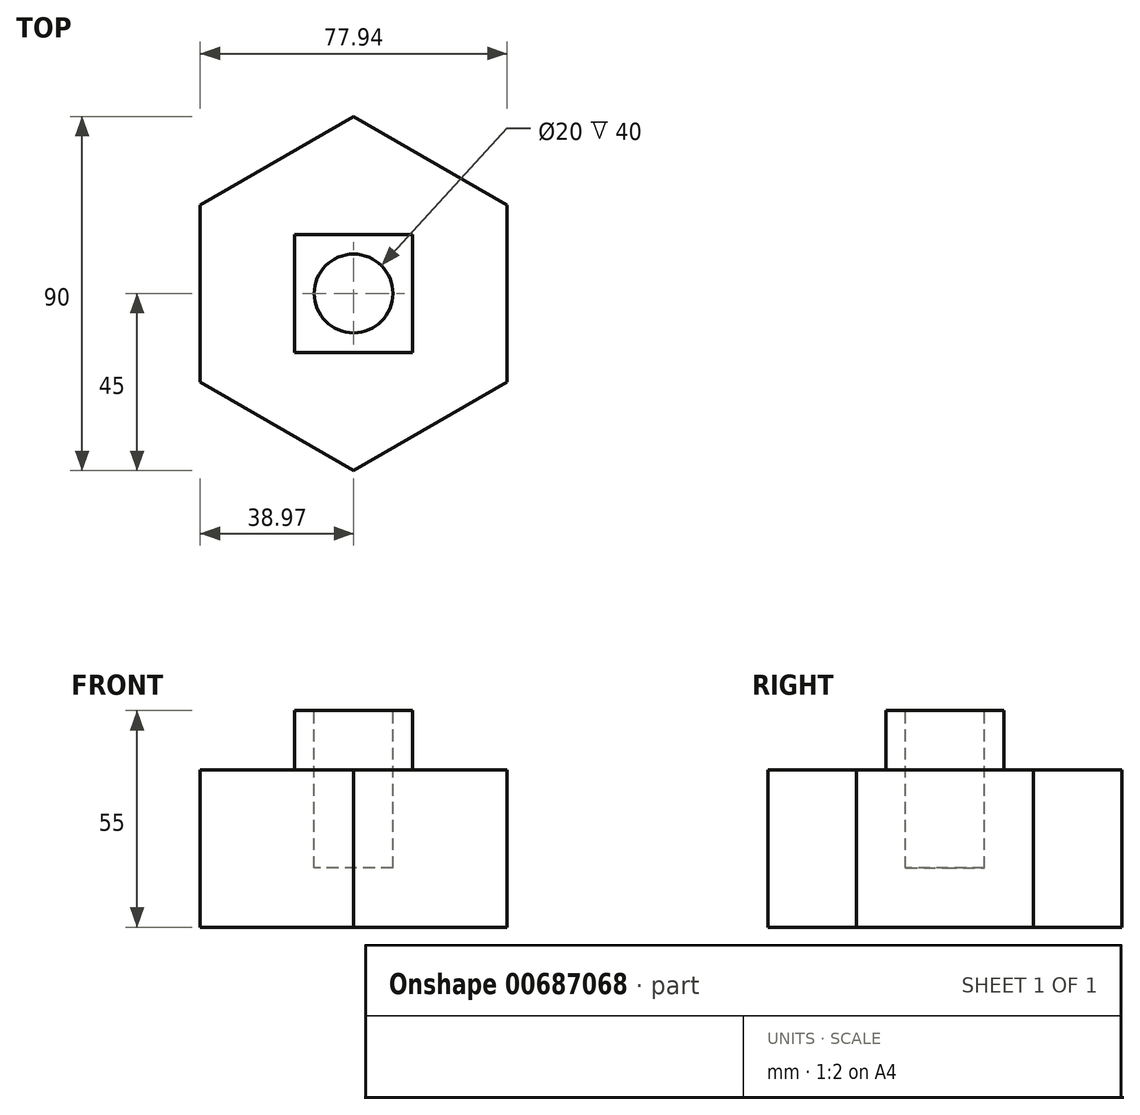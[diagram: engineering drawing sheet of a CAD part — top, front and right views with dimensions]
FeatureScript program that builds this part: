
annotation { "Feature Type Name" : "Feature", "Feature Type Description" : "" }
export const myFeature = defineFeature(function(context is Context, id is Id, definition is map)
    precondition{}
    {
        {
            var Q0;
            Q0=qCreatedBy(makeId("Top.planeOp"),FACE);
            var sketch = newSketch(context, id + "F0", { "sketchPlane" : qUnion([Q0])});
            skCircle(sketch, "E0.cCircle", {"center": v(0, 0) * mm, "radius": 38.97 * mm, "construction": true});
            skLineSegment(sketch, "E0.0", {"start": v(38.97, 22.5) * mm, "end": v(38.97, -22.5) * mm});
            skLineSegment(sketch, "E0.1", {"start": v(38.97, -22.5) * mm, "end": v(0, -45) * mm});
            skLineSegment(sketch, "E0.2", {"start": v(0, -45) * mm, "end": v(-38.97, -22.5) * mm});
            skLineSegment(sketch, "E0.3", {"start": v(-38.97, -22.5) * mm, "end": v(-38.97, 22.5) * mm});
            skLineSegment(sketch, "E0.4", {"start": v(-38.97, 22.5) * mm, "end": v(0, 45) * mm});
            skLineSegment(sketch, "E0.5", {"start": v(0, 45) * mm, "end": v(38.97, 22.5) * mm});
            skPoint(sketch, "E0.0.midPoint", {"position": v(38.97, 0) * mm});
            skSolve(sketch);
        }
        {
            var Q0;
            Q0 = qSketchRegion(id + "F0", true);
            extrude(context, id + "F1", {"entities" : qUnion([Q0]), "depth" : 40 * mm, "offsetDistance" : 25 * mm});
        }
        {
            var Q0;
            Q0=makeQuery(id+"F1.opExtrude","CAP_FACE",FACE,{"disambiguationData":[OSD([sQuery(id+"F0.wireOp",EDGE,"E0.0"),sQuery(id+"F0.wireOp",EDGE,"E0.1"),sQuery(id+"F0.wireOp",EDGE,"E0.2"),sQuery(id+"F0.wireOp",EDGE,"E0.3"),sQuery(id+"F0.wireOp",EDGE,"E0.4"),sQuery(id+"F0.wireOp",EDGE,"E0.5")])],"isStart":false});
            var sketch = newSketch(context, id + "F2", { "sketchPlane" : qUnion([Q0])});
            skLineSegment(sketch, "E1.bottom", {"start": v(15, 15) * mm, "end": v(-15, 15) * mm});
            skLineSegment(sketch, "E1.top", {"start": v(15, -15) * mm, "end": v(-15, -15) * mm});
            skLineSegment(sketch, "E1.left", {"start": v(15, 15) * mm, "end": v(15, -15) * mm});
            skLineSegment(sketch, "E1.right", {"start": v(-15, 15) * mm, "end": v(-15, -15) * mm});
            skPoint(sketch, "E1.middle", {"position": v(0, 0) * mm});
            skSolve(sketch);
        }
        {
            var Q0;
            Q0=makeQuery(id+"F2.imprint","IMPRINT",FACE,{"disambiguationData":[TD([[makeQuery(id+"F2.imprint","IMPRINT",EDGE,{"derivedFrom":sQuery(id+"F2.wireOp",EDGE,"E1.bottom")}),1.0]])]});
            extrude(context, id + "F3", {"entities" : qUnion([Q0]), "operationType" : NewBodyOperationType.ADD, "depth" : 15 * mm, "offsetDistance" : 25 * mm});
        }
        {
            var Q0;
            Q0=makeQuery(id+"F3.opExtrude","CAP_FACE",FACE,{"disambiguationData":[OSD([sQuery(id+"F2.wireOp",EDGE,"E1.bottom"),sQuery(id+"F2.wireOp",EDGE,"E1.top"),sQuery(id+"F2.wireOp",EDGE,"E1.left"),sQuery(id+"F2.wireOp",EDGE,"E1.right")])],"isStart":false});
            var sketch = newSketch(context, id + "F4", { "sketchPlane" : qUnion([Q0])});
            skCircle(sketch, "E2", {"center": v(0, 0) * mm, "radius": 10 * mm});
            skSolve(sketch);
        }
        {
            var Q0;
            Q0=makeQuery(id+"F4.imprint","IMPRINT",FACE,{"disambiguationData":[TD([[makeQuery(id+"F4.imprint","IMPRINT",EDGE,{"derivedFrom":sQuery(id+"F4.wireOp",EDGE,"E2")}),1.0]])]});
            extrude(context, id + "F5", {"entities" : qUnion([Q0]), "operationType" : NewBodyOperationType.REMOVE, "oppositeDirection" : true, "depth" : 40 * mm, "offsetDistance" : 25 * mm});
        }
    });
